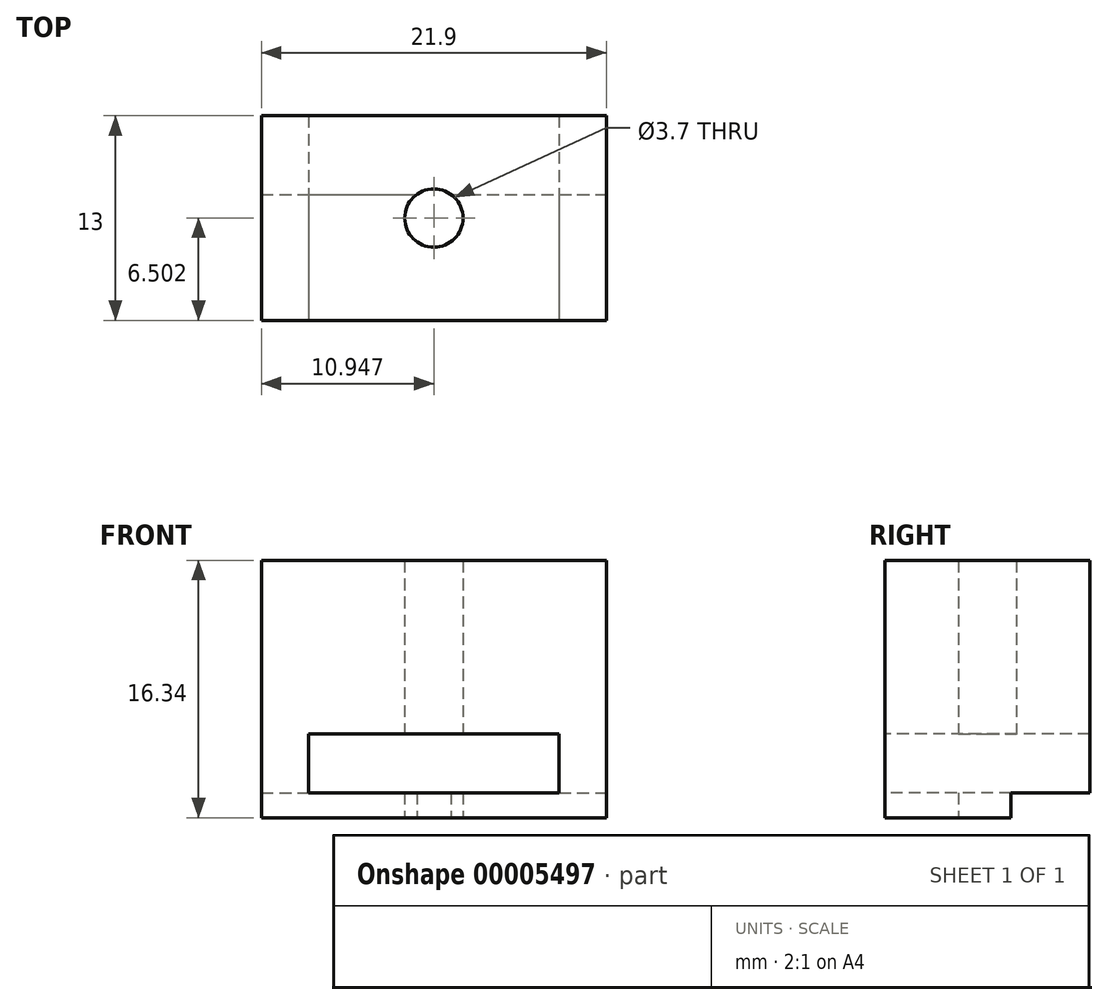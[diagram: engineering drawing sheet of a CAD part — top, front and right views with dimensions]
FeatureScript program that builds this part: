
annotation { "Feature Type Name" : "Feature", "Feature Type Description" : "" }
export const myFeature = defineFeature(function(context is Context, id is Id, definition is map)
    precondition{}
    {
        {
            var Q0;
            Q0=qCreatedBy(makeId("Top.planeOp"),FACE);
            var sketch = newSketch(context, id + "F0", { "sketchPlane" : qUnion([Q0])});
            skLineSegment(sketch, "E0.bottom", {"start": v(-6.93, 24.15) * mm, "end": v(8.97, 24.15) * mm});
            skLineSegment(sketch, "E0.top", {"start": v(-6.93, 11.15) * mm, "end": v(8.97, 11.15) * mm});
            skLineSegment(sketch, "E1", {"start": v(1.02, 24.15) * mm, "end": v(1.02, 11.15) * mm, "construction": true});
            skCircle(sketch, "E2", {"center": v(1.02, 17.65) * mm, "radius": 1.85 * mm});
            skCircle(sketch, "E3", {"center": v(1.02, 17.65) * mm, "radius": 6.5 * mm, "construction": true});
            skLineSegment(sketch, "E4", {"start": v(-6.93, 24.15) * mm, "end": v(-9.93, 24.15) * mm});
            skLineSegment(sketch, "E5", {"start": v(-9.93, 24.15) * mm, "end": v(-9.93, 11.15) * mm});
            skLineSegment(sketch, "E6", {"start": v(-6.93, 11.15) * mm, "end": v(-9.93, 11.15) * mm});
            skLineSegment(sketch, "E7", {"start": v(8.97, 24.15) * mm, "end": v(11.97, 24.15) * mm});
            skLineSegment(sketch, "E8", {"start": v(8.97, 11.15) * mm, "end": v(11.97, 11.15) * mm});
            skLineSegment(sketch, "E9", {"start": v(11.97, 24.15) * mm, "end": v(11.97, 11.15) * mm});
            skSolve(sketch);
        }
        {
            var Q0;
            Q0 = qSketchRegion(id + "F0", true);
            extrude(context, id + "F1", {"entities" : qUnion([Q0]), "depth" : 2.4 * mm});
        }
        {
            var Q0;
            Q0=makeQuery(id+"F1.opExtrude","CAP_FACE",FACE,{"disambiguationData":[OSD([sQuery(id+"F0.wireOp",EDGE,"E0.bottom"),sQuery(id+"F0.wireOp",EDGE,"E0.top"),sQuery(id+"F0.wireOp",EDGE,"E2"),sQuery(id+"F0.wireOp",EDGE,"E4"),sQuery(id+"F0.wireOp",EDGE,"E5"),sQuery(id+"F0.wireOp",EDGE,"E6"),sQuery(id+"F0.wireOp",EDGE,"E7"),sQuery(id+"F0.wireOp",EDGE,"E8"),sQuery(id+"F0.wireOp",EDGE,"E9")])],"isStart":false});
            var sketch = newSketch(context, id + "F2", { "sketchPlane" : qUnion([Q0])});
            skLineSegment(sketch, "E10.bottom", {"start": v(-9.93, 24.15) * mm, "end": v(-6.93, 24.15) * mm});
            skLineSegment(sketch, "E10.top", {"start": v(-9.93, 11.15) * mm, "end": v(-6.93, 11.15) * mm});
            skLineSegment(sketch, "E10.left", {"start": v(-9.93, 24.15) * mm, "end": v(-9.93, 11.15) * mm});
            skLineSegment(sketch, "E10.right", {"start": v(-6.93, 24.15) * mm, "end": v(-6.93, 11.15) * mm});
            skLineSegment(sketch, "E11.bottom", {"start": v(11.97, 24.15) * mm, "end": v(8.97, 24.15) * mm});
            skLineSegment(sketch, "E11.top", {"start": v(11.97, 11.15) * mm, "end": v(8.97, 11.15) * mm});
            skLineSegment(sketch, "E11.left", {"start": v(11.97, 24.15) * mm, "end": v(11.97, 11.15) * mm});
            skLineSegment(sketch, "E11.right", {"start": v(8.97, 24.15) * mm, "end": v(8.97, 11.15) * mm});
            skSolve(sketch);
        }
        {
            var Q0;
            Q0 = qSketchRegion(id + "F2", true);
            extrude(context, id + "F3", {"entities" : qUnion([Q0]), "operationType" : NewBodyOperationType.ADD, "depth" : 3.75 * mm});
        }
        {
            var Q0;
            Q0=makeQuery(id+"F1.opExtrude","CAP_FACE",FACE,{"disambiguationData":[OSD([sQuery(id+"F0.wireOp",EDGE,"E0.bottom"),sQuery(id+"F0.wireOp",EDGE,"E0.top"),sQuery(id+"F0.wireOp",EDGE,"E2"),sQuery(id+"F0.wireOp",EDGE,"E4"),sQuery(id+"F0.wireOp",EDGE,"E5"),sQuery(id+"F0.wireOp",EDGE,"E6"),sQuery(id+"F0.wireOp",EDGE,"E7"),sQuery(id+"F0.wireOp",EDGE,"E8"),sQuery(id+"F0.wireOp",EDGE,"E9")])],"isStart":true});
            var sketch = newSketch(context, id + "F4", { "sketchPlane" : qUnion([Q0])});
            skCircle(sketch, "E12", {"center": v(1.02, -17.65) * mm, "radius": 6.5 * mm});
            skSolve(sketch);
        }
        {
            var Q0;
            Q0=makeQuery(id+"F3.boolean.opBoolean","MERGE",FACE,{"derivedFrom":[makeQuery(id+"F1.opExtrude","SWEPT_FACE",FACE,{"disambiguationData":[OSD([sQuery(id+"F0.wireOp",EDGE,"E5")])]}),makeQuery(id+"F3.opExtrude","SWEPT_FACE",FACE,{"disambiguationData":[OSD([sQuery(id+"F2.wireOp",EDGE,"E10.left")])]})]});
            var sketch = newSketch(context, id + "F5", { "sketchPlane" : qUnion([Q0])});
            skLineSegment(sketch, "E13.0", {"start": v(-11.15, -5) * mm, "end": v(-24.15, -5) * mm, "construction": true});
            skLineSegment(sketch, "E14.0", {"start": v(-11.15, 0) * mm, "end": v(-24.15, 0) * mm, "construction": true});
            skLineSegment(sketch, "E15", {"start": v(-24.15, -2.5) * mm, "end": v(-24.15, -5) * mm, "construction": true});
            skLineSegment(sketch, "E16", {"start": v(-24.15, -2.5) * mm, "end": v(-29.8, -2.5) * mm, "construction": true});
            skArc(sketch, "E17", {"start": v(-24.23, 0) * mm, "mid": v(-21.02, -5.55) * mm, "end": v(-22.22, 0.75) * mm});
            skLineSegment(sketch, "E18", {"start": v(-22.09, 0.75) * mm, "end": v(-25.9, 0.75) * mm});
            skLineSegment(sketch, "E19", {"start": v(-25.9, 0.75) * mm, "end": v(-25.9, 0) * mm});
            skLineSegment(sketch, "E20", {"start": v(-25.9, 0) * mm, "end": v(-24.23, 0) * mm});
            skSolve(sketch);
        }
        {
            var Q0;
            Q0 = qSketchRegion(id + "F5", true);
            extrude(context, id + "F6", {"entities" : qUnion([Q0]), "operationType" : NewBodyOperationType.REMOVE, "oppositeDirection" : true, "depth" : 25 * mm});
        }
        {
            var Q0;
            Q0=makeQuery(id+"F3.opExtrude","CAP_FACE",FACE,{"disambiguationData":[OSD([sQuery(id+"F2.wireOp",EDGE,"E11.bottom"),sQuery(id+"F2.wireOp",EDGE,"E11.top"),sQuery(id+"F2.wireOp",EDGE,"E11.left"),sQuery(id+"F2.wireOp",EDGE,"E11.right")])],"isStart":false});
            var sketch = newSketch(context, id + "F7", { "sketchPlane" : qUnion([Q0])});
            skLineSegment(sketch, "E21.0", {"start": v(-9.93, 24.15) * mm, "end": v(-9.93, 11.15) * mm});
            skLineSegment(sketch, "E22.0", {"start": v(11.97, 24.15) * mm, "end": v(11.97, 11.15) * mm});
            skLineSegment(sketch, "E23", {"start": v(-9.93, 11.15) * mm, "end": v(11.97, 11.15) * mm});
            skLineSegment(sketch, "E24", {"start": v(11.97, 24.15) * mm, "end": v(-9.93, 24.15) * mm});
            skSolve(sketch);
        }
        {
            var Q0;
            Q0 = qSketchRegion(id + "F7", true);
            extrude(context, id + "F8", {"entities" : qUnion([Q0]), "operationType" : NewBodyOperationType.ADD, "depth" : 3 * mm});
        }
        {
            var Q0;
            Q0=makeQuery(id+"F8.opExtrude","CAP_FACE",FACE,{"disambiguationData":[OSD([sQuery(id+"F7.wireOp",EDGE,"E21.0"),sQuery(id+"F7.wireOp",EDGE,"E22.0"),sQuery(id+"F7.wireOp",EDGE,"E23"),sQuery(id+"F7.wireOp",EDGE,"E24")])],"isStart":true});
            var sketch = newSketch(context, id + "F9", { "sketchPlane" : qUnion([Q0])});
            skCircle(sketch, "E25.0", {"center": v(1.02, -17.65) * mm, "radius": 1.85 * mm});
            skSolve(sketch);
        }
        {
            var Q0;
            Q0 = qSketchRegion(id + "F9", true);
            extrude(context, id + "F10", {"entities" : qUnion([Q0]), "operationType" : NewBodyOperationType.REMOVE, "oppositeDirection" : true, "depth" : 25 * mm});
        }
        {
            var Q0;
            Q0=makeQuery(id+"F8.boolean.opBoolean","MERGE",FACE,{"derivedFrom":[makeQuery(id+"F3.boolean.opBoolean","MERGE",FACE,{"derivedFrom":[makeQuery(id+"F1.opExtrude","SWEPT_FACE",FACE,{"disambiguationData":[OSD([sQuery(id+"F0.wireOp",EDGE,"E9")])]}),makeQuery(id+"F3.opExtrude","SWEPT_FACE",FACE,{"disambiguationData":[OSD([sQuery(id+"F2.wireOp",EDGE,"E11.left")])]})]}),makeQuery(id+"F8.opExtrude","SWEPT_FACE",FACE,{"disambiguationData":[OSD([sQuery(id+"F7.wireOp",EDGE,"E22.0")])]})]});
            var sketch = newSketch(context, id + "F11", { "sketchPlane" : qUnion([Q0])});
            skLineSegment(sketch, "E26.0", {"start": v(24.15, 0) * mm, "end": v(11.15, 0) * mm});
            skLineSegment(sketch, "E27", {"start": v(11.15, 0) * mm, "end": v(11.15, 0.8) * mm});
            skLineSegment(sketch, "E28", {"start": v(11.15, 0.8) * mm, "end": v(24.15, 0.8) * mm});
            skLineSegment(sketch, "E29", {"start": v(24.15, 0.8) * mm, "end": v(24.15, 0) * mm});
            skSolve(sketch);
        }
        {
            var Q0;
            Q0 = qSketchRegion(id + "F11", true);
            extrude(context, id + "F12", {"entities" : qUnion([Q0]), "operationType" : NewBodyOperationType.REMOVE, "oppositeDirection" : true, "depth" : 25 * mm});
        }
        {
            var Q0;
            Q0=makeQuery(id+"F12.boolean.opBoolean","COPY",FACE,{"derivedFrom":makeQuery(id+"F12.opExtrude","SWEPT_FACE",FACE,{"disambiguationData":[OSD([sQuery(id+"F11.wireOp",EDGE,"E28")])]})});
            var sketch = newSketch(context, id + "F13", { "sketchPlane" : qUnion([Q0])});
            skLineSegment(sketch, "E30.0", {"start": v(-9.93, -24.15) * mm, "end": v(11.97, -24.15) * mm});
            skLineSegment(sketch, "E31", {"start": v(-9.93, -24.15) * mm, "end": v(-9.93, -19.15) * mm});
            skLineSegment(sketch, "E32", {"start": v(-9.93, -19.15) * mm, "end": v(11.97, -19.15) * mm});
            skLineSegment(sketch, "E33", {"start": v(11.97, -24.15) * mm, "end": v(11.97, -19.15) * mm});
            skSolve(sketch);
        }
        {
            var Q0;
            Q0 = qSketchRegion(id + "F13", true);
            var Q1;
            Q1=makeQuery(id+"F1.opExtrude","CAP_FACE",FACE,{"disambiguationData":[OSD([sQuery(id+"F0.wireOp",EDGE,"E0.bottom"),sQuery(id+"F0.wireOp",EDGE,"E0.top"),sQuery(id+"F0.wireOp",EDGE,"E2"),sQuery(id+"F0.wireOp",EDGE,"E4"),sQuery(id+"F0.wireOp",EDGE,"E5"),sQuery(id+"F0.wireOp",EDGE,"E6"),sQuery(id+"F0.wireOp",EDGE,"E7"),sQuery(id+"F0.wireOp",EDGE,"E8"),sQuery(id+"F0.wireOp",EDGE,"E9")])],"isStart":false});
            extrude(context, id + "F14", {"entities" : qUnion([Q0]), "operationType" : NewBodyOperationType.REMOVE, "endBound" : BoundingType.UP_TO_SURFACE, "oppositeDirection" : true, "endBoundEntityFace" : qUnion([Q1]), "depth" : 1.6 * mm});
        }
        {
            var Q0;
            Q0=makeQuery(id+"F8.opExtrude","CAP_FACE",FACE,{"disambiguationData":[OSD([sQuery(id+"F7.wireOp",EDGE,"E21.0"),sQuery(id+"F7.wireOp",EDGE,"E22.0"),sQuery(id+"F7.wireOp",EDGE,"E23"),sQuery(id+"F7.wireOp",EDGE,"E24")])],"isStart":false});
            var sketch = newSketch(context, id + "F15", { "sketchPlane" : qUnion([Q0])});
            skLineSegment(sketch, "E34.0.0", {"start": v(11.97, 24.15) * mm, "end": v(-9.93, 24.15) * mm});
            skLineSegment(sketch, "E34.0.1", {"start": v(-9.93, 24.15) * mm, "end": v(-9.93, 11.15) * mm});
            skLineSegment(sketch, "E34.0.2", {"start": v(-9.93, 11.15) * mm, "end": v(11.97, 11.15) * mm});
            skLineSegment(sketch, "E34.0.3", {"start": v(11.97, 24.15) * mm, "end": v(11.97, 11.15) * mm});
            skCircle(sketch, "E35.0", {"center": v(1.02, 17.65) * mm, "radius": 1.85 * mm});
            skSolve(sketch);
        }
        {
            var Q0;
            Q0 = qSketchRegion(id + "F15", true);
            extrude(context, id + "F16", {"entities" : qUnion([Q0]), "operationType" : NewBodyOperationType.ADD, "depth" : 8 * mm});
        }
    });
